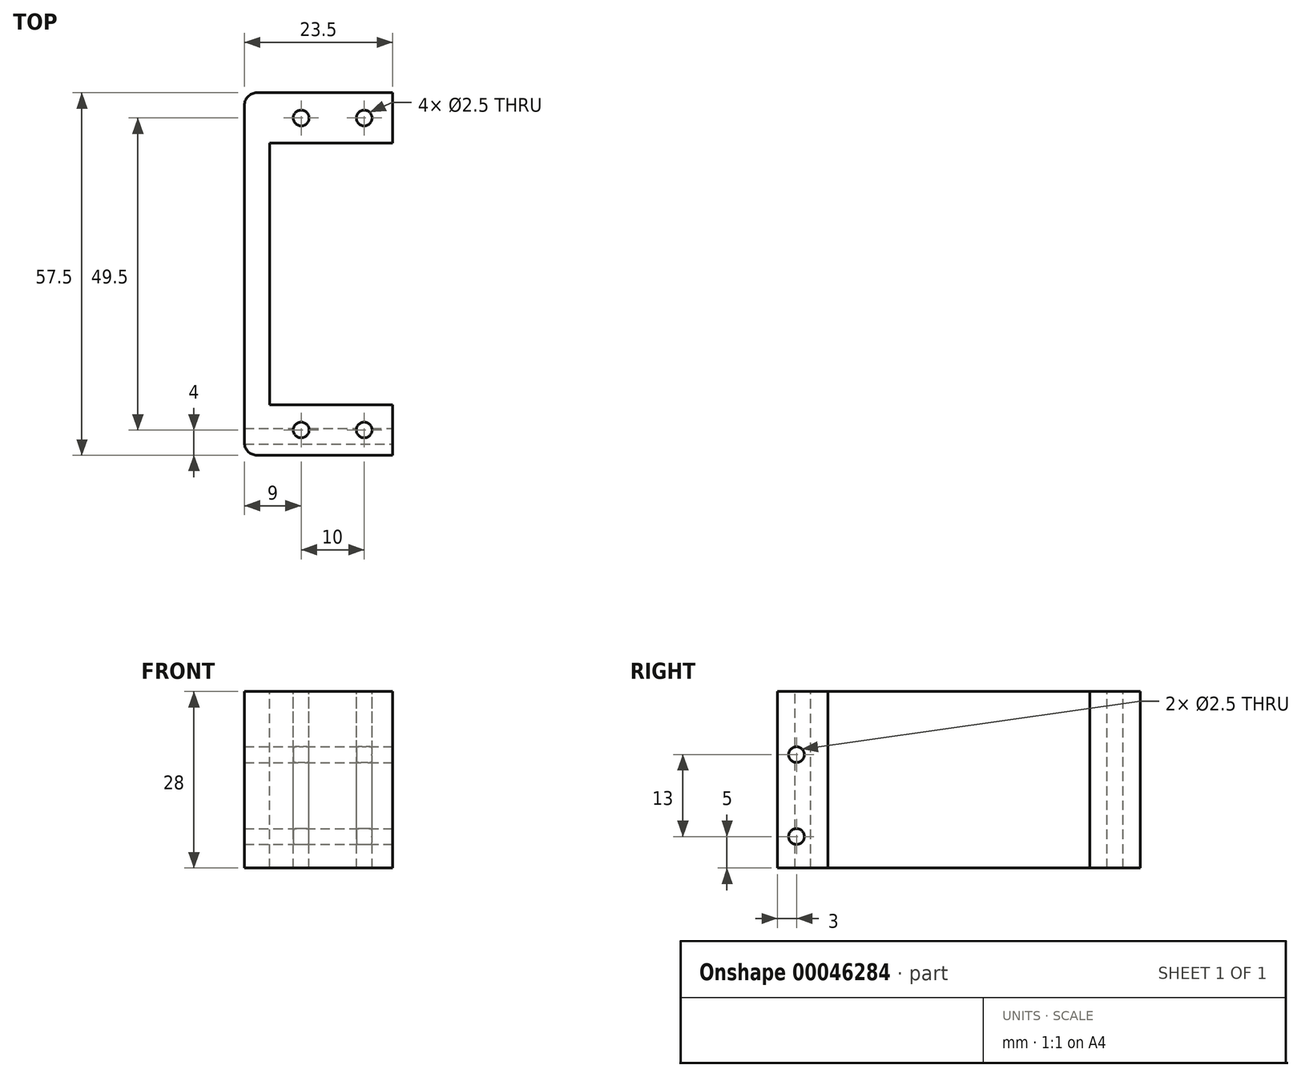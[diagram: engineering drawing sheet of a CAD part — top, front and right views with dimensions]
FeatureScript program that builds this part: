
annotation { "Feature Type Name" : "Feature", "Feature Type Description" : "" }
export const myFeature = defineFeature(function(context is Context, id is Id, definition is map)
    precondition{}
    {
        {
            var Q0;
            Q0=qCreatedBy(makeId("Top.planeOp"),FACE);
            var sketch = newSketch(context, id + "F0", { "sketchPlane" : qUnion([Q0])});
            skLineSegment(sketch, "E0.bottom", {"start": v(0, 20.75) * mm, "end": v(-19.5, 20.75) * mm});
            skLineSegment(sketch, "E0.top", {"start": v(0, -20.75) * mm, "end": v(-19.5, -20.75) * mm});
            skLineSegment(sketch, "E0.left", {"start": v(0, 20.75) * mm, "end": v(0, -20.75) * mm});
            skLineSegment(sketch, "E0.right", {"start": v(-19.5, 20.75) * mm, "end": v(-19.5, -20.75) * mm});
            skLineSegment(sketch, "E1", {"start": v(0, 28.75) * mm, "end": v(-23.5, 28.75) * mm});
            skLineSegment(sketch, "E2", {"start": v(-23.5, 28.75) * mm, "end": v(-23.5, -28.75) * mm});
            skLineSegment(sketch, "E3", {"start": v(-23.5, -28.75) * mm, "end": v(0, -28.75) * mm});
            skCircle(sketch, "E4", {"center": v(-4.5, 24.75) * mm, "radius": 1.25 * mm});
            skCircle(sketch, "E5", {"center": v(-14.5, 24.75) * mm, "radius": 1.25 * mm});
            skCircle(sketch, "E6.MirrorC", {"center": v(-4.5, -24.75) * mm, "radius": 1.25 * mm});
            skCircle(sketch, "E7.MirrorC", {"center": v(-14.5, -24.75) * mm, "radius": 1.25 * mm});
            skLineSegment(sketch, "E8", {"start": v(0, 28.75) * mm, "end": v(0, 20.75) * mm});
            skLineSegment(sketch, "E9", {"start": v(0, -28.75) * mm, "end": v(0, -20.75) * mm});
            skSolve(sketch);
        }
        {
            var Q0;
            Q0=makeQuery(id+"F0.imprint","IMPRINT",FACE,{"disambiguationData":[TD([[makeQuery(id+"F0.imprint","IMPRINT",EDGE,{"derivedFrom":sQuery(id+"F0.wireOp",EDGE,"E0.bottom")}),-1.0]])]});
            extrude(context, id + "F1", {"entities" : qUnion([Q0]), "oppositeDirection" : true, "depth" : 28 * mm});
        }
        {
            var Q0;
            Q0=makeQuery(id+"F1.opExtrude","SWEPT_FACE",FACE,{"disambiguationData":[OSD([sQuery(id+"F0.wireOp",EDGE,"E9")])]});
            var sketch = newSketch(context, id + "F2", { "sketchPlane" : qUnion([Q0])});
            skCircle(sketch, "E10", {"center": v(-25.75, -10) * mm, "radius": 1.25 * mm});
            skCircle(sketch, "E11", {"center": v(-25.75, -23) * mm, "radius": 1.25 * mm});
            skCircle(sketch, "E12.MirrorC", {"center": v(25.75, -23) * mm, "radius": 1.25 * mm});
            skCircle(sketch, "E13.MirrorC", {"center": v(25.75, -10) * mm, "radius": 1.25 * mm});
            skSolve(sketch);
        }
        {
            var Q0;
            Q0=makeQuery(id+"F2.imprint","IMPRINT",FACE,{"disambiguationData":[TD([[makeQuery(id+"F2.imprint","IMPRINT",EDGE,{"derivedFrom":sQuery(id+"F2.wireOp",EDGE,"E10")}),1.0]])]});
            var Q1;
            Q1=makeQuery(id+"F2.imprint","IMPRINT",FACE,{"disambiguationData":[TD([[makeQuery(id+"F2.imprint","IMPRINT",EDGE,{"derivedFrom":sQuery(id+"F2.wireOp",EDGE,"E11")}),1.0]])]});
            var Q2;
            Q2=makeQuery(id+"F2.imprint","IMPRINT",FACE,{"disambiguationData":[TD([[makeQuery(id+"F2.imprint","IMPRINT",EDGE,{"derivedFrom":sQuery(id+"F2.wireOp",EDGE,"E13.MirrorC")}),-1.0]])]});
            var Q3;
            Q3=makeQuery(id+"F2.imprint","IMPRINT",FACE,{"disambiguationData":[TD([[makeQuery(id+"F2.imprint","IMPRINT",EDGE,{"derivedFrom":sQuery(id+"F2.wireOp",EDGE,"E12.MirrorC")}),-1.0]])]});
            extrude(context, id + "F3", {"entities" : qUnion([Q0, Q1, Q2, Q3]), "operationType" : NewBodyOperationType.REMOVE, "endBound" : BoundingType.THROUGH_ALL, "oppositeDirection" : true, "depth" : 25 * mm});
        }
        {
            var Q0;
            Q0=makeQuery(id+"F1.opExtrude","SWEPT_EDGE",EDGE,{"disambiguationData":[OSD([sQuery(id+"F0.wireOp",EDGE,"E2"),sQuery(id+"F0.wireOp",EDGE,"E3")])]});
            var Q1;
            Q1=makeQuery(id+"F1.opExtrude","SWEPT_EDGE",EDGE,{"disambiguationData":[OSD([sQuery(id+"F0.wireOp",EDGE,"E1"),sQuery(id+"F0.wireOp",EDGE,"E2")])]});
            fillet(context, id + "F4", {"entities" : qUnion([Q0, Q1]), "radius" : 2 * mm, "tangentPropagation" : true, "allowEdgeOverflow" : false});
        }
    });
